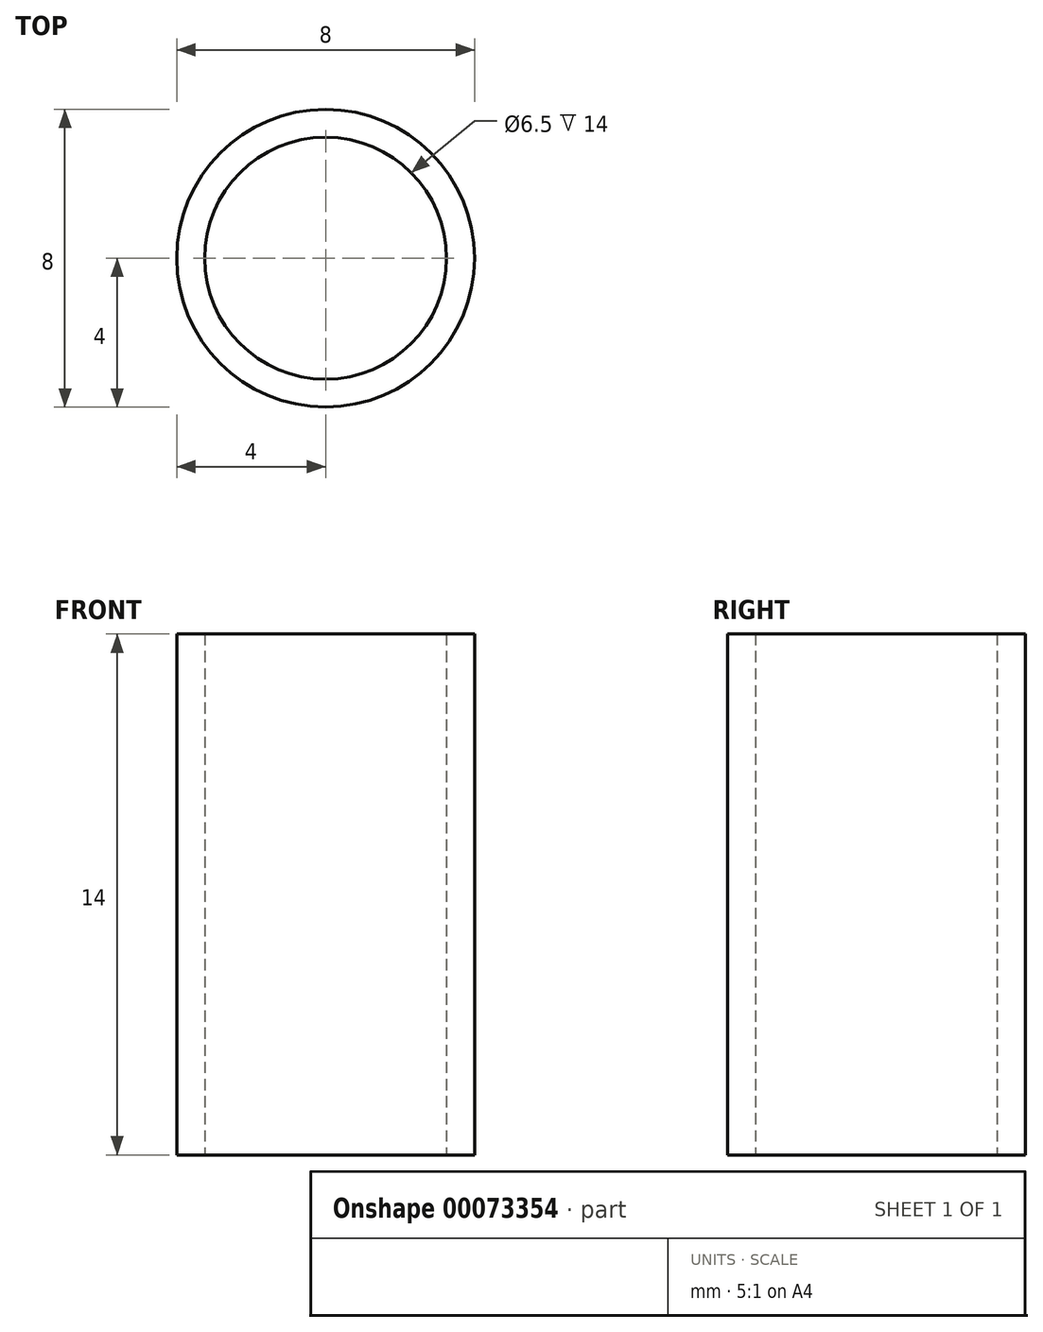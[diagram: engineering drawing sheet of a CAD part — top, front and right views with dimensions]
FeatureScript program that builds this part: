
annotation { "Feature Type Name" : "Feature", "Feature Type Description" : "" }
export const myFeature = defineFeature(function(context is Context, id is Id, definition is map)
    precondition{}
    {
        {
            var Q0;
            Q0=qCreatedBy(makeId("Top.planeOp"),FACE);
            var sketch = newSketch(context, id + "F0", { "sketchPlane" : qUnion([Q0])});
            skCircle(sketch, "E0", {"center": v(0, 0) * mm, "radius": 4 * mm});
            skCircle(sketch, "E1", {"center": v(0, 0) * mm, "radius": 3.25 * mm});
            skSolve(sketch);
        }
        {
            var Q0;
            Q0=makeQuery(id+"F0.imprint","IMPRINT",FACE,{"disambiguationData":[TD([[makeQuery(id+"F0.imprint","IMPRINT",EDGE,{"derivedFrom":sQuery(id+"F0.wireOp",EDGE,"E0")}),1.0]])]});
            extrude(context, id + "F1", {"entities" : qUnion([Q0]), "depth" : 14 * mm, "offsetDistance" : 25 * mm});
        }
    });
